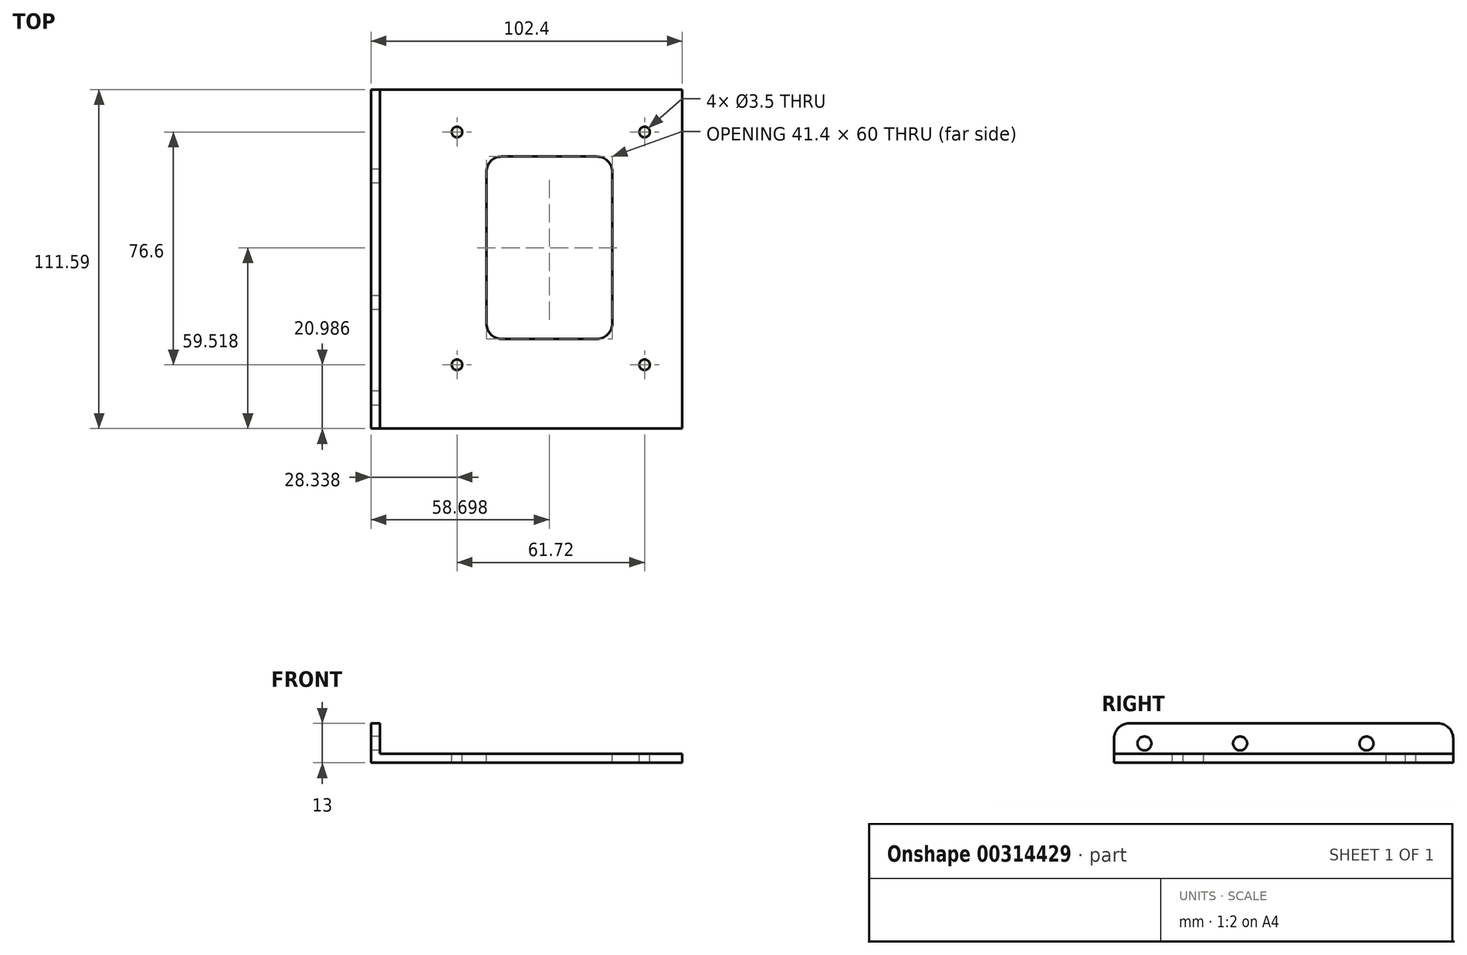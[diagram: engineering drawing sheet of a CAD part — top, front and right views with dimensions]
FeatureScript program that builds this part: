
annotation { "Feature Type Name" : "Feature", "Feature Type Description" : "" }
export const myFeature = defineFeature(function(context is Context, id is Id, definition is map)
    precondition{}
    {
        {
            var Q0;
            Q0=qCreatedBy(makeId("Top.planeOp"),FACE);
            var sketch = newSketch(context, id + "F0", { "sketchPlane" : qUnion([Q0])});
            skLineSegment(sketch, "E0.bottom", {"start": v(-63.5, 99.79) * mm, "end": v(38.9, 99.79) * mm});
            skLineSegment(sketch, "E0.top", {"start": v(-63.5, -47.21) * mm, "end": v(38.9, -47.21) * mm});
            skLineSegment(sketch, "E0.left", {"start": v(-63.5, 99.79) * mm, "end": v(-63.5, -47.21) * mm});
            skLineSegment(sketch, "E0.right", {"start": v(38.9, 99.79) * mm, "end": v(38.9, -47.21) * mm});
            skSolve(sketch);
        }
        {
            var Q0;
            Q0=qSketchRegion(id+"F0",true);
            extrude(context, id + "F1", {"entities" : qUnion([Q0]), "depth" : 3 * mm});
        }
        {
            var Q0;
            Q0=makeQuery(id+"F1.opExtrude","CAP_FACE",FACE,{"disambiguationData":[OSD([sQuery(id+"F0.wireOp",EDGE,"E0.bottom"),sQuery(id+"F0.wireOp",EDGE,"E0.top"),sQuery(id+"F0.wireOp",EDGE,"E0.left"),sQuery(id+"F0.wireOp",EDGE,"E0.right")])],"isStart":false});
            var sketch = newSketch(context, id + "F2", { "sketchPlane" : qUnion([Q0])});
            skLineSegment(sketch, "E1.bottom", {"start": v(-63.5, -47.21) * mm, "end": v(-60.5, -47.21) * mm});
            skLineSegment(sketch, "E1.top", {"start": v(-63.5, 99.79) * mm, "end": v(-60.5, 99.79) * mm});
            skLineSegment(sketch, "E1.left", {"start": v(-63.5, -47.21) * mm, "end": v(-63.5, 99.79) * mm});
            skLineSegment(sketch, "E1.right", {"start": v(-60.5, -47.21) * mm, "end": v(-60.5, 99.79) * mm});
            skSolve(sketch);
        }
        {
            var Q0;
            Q0=qSketchRegion(id+"F2",true);
            extrude(context, id + "F3", {"entities" : qUnion([Q0]), "operationType" : NewBodyOperationType.ADD, "depth" : 10 * mm});
        }
        {
            var Q0;
            Q0=makeQuery(id+"F1.opExtrude","SWEPT_FACE",FACE,{"disambiguationData":[OSD([sQuery(id+"F0.wireOp",EDGE,"E0.right")])]});
            var Q1;
            Q1=makeQuery(id+"F3.boolean.opBoolean","MERGE",FACE,{"derivedFrom":[makeQuery(id+"F1.opExtrude","SWEPT_FACE",FACE,{"disambiguationData":[OSD([sQuery(id+"F0.wireOp",EDGE,"E0.left")])]}),makeQuery(id+"F3.opExtrude","SWEPT_FACE",FACE,{"disambiguationData":[OSD([sQuery(id+"F2.wireOp",EDGE,"E1.left")])]})]});
            cPlane(context, id + "F4", {"entities" : qUnion([Q0, Q1]), "cplaneType" : CPlaneType.MID_PLANE, "offset" : 25 * mm, "width" : 150 * mm, "height" : 150 * mm});
        }
        {
            var Q0;
            Q0=makeQuery(id+"F3.boolean.opBoolean","MERGE",FACE,{"derivedFrom":[makeQuery(id+"F1.opExtrude","SWEPT_FACE",FACE,{"disambiguationData":[OSD([sQuery(id+"F0.wireOp",EDGE,"E0.left")])]}),makeQuery(id+"F3.opExtrude","SWEPT_FACE",FACE,{"disambiguationData":[OSD([sQuery(id+"F2.wireOp",EDGE,"E1.left")])]})]});
            var sketch = newSketch(context, id + "F5", { "sketchPlane" : qUnion([Q0])});
            skCircle(sketch, "E2", {"center": v(1.81, 6.35) * mm, "radius": 2.3 * mm});
            skCircle(sketch, "E3", {"center": v(-29.68, 6.35) * mm, "radius": 2.3 * mm});
            skCircle(sketch, "E4", {"center": v(-71.29, 6.35) * mm, "radius": 2.3 * mm});
            skSolve(sketch);
        }
        {
            var Q0;
            Q0=qSketchRegion(id+"F5",true);
            extrude(context, id + "F6", {"entities" : qUnion([Q0]), "operationType" : NewBodyOperationType.REMOVE, "endBound" : BoundingType.THROUGH_ALL, "oppositeDirection" : true, "depth" : 25 * mm});
        }
        {
            var Q0;
            Q0=makeQuery(id+"F1.opExtrude","CAP_FACE",FACE,{"disambiguationData":[OSD([sQuery(id+"F0.wireOp",EDGE,"E0.bottom"),sQuery(id+"F0.wireOp",EDGE,"E0.top"),sQuery(id+"F0.wireOp",EDGE,"E0.left"),sQuery(id+"F0.wireOp",EDGE,"E0.right")])],"isStart":false});
            var sketch = newSketch(context, id + "F7", { "sketchPlane" : qUnion([Q0])});
            skCircle(sketch, "E5", {"center": v(18.56, 85.79) * mm, "radius": 1.75 * mm});
            skCircle(sketch, "E6", {"center": v(-43.16, 85.79) * mm, "radius": 1.75 * mm});
            skCircle(sketch, "E7", {"center": v(18.56, 9.19) * mm, "radius": 1.75 * mm});
            skCircle(sketch, "E8", {"center": v(-43.16, 9.19) * mm, "radius": 1.75 * mm});
            skCircle(sketch, "E9.1.0.0", {"center": v(26.56, 85.79) * mm, "radius": 1.75 * mm});
            skCircle(sketch, "E9.1.0.1", {"center": v(-35.16, 85.79) * mm, "radius": 1.75 * mm});
            skCircle(sketch, "E9.1.0.2", {"center": v(-35.16, 9.19) * mm, "radius": 1.75 * mm});
            skCircle(sketch, "E9.1.0.3", {"center": v(26.56, 9.19) * mm, "radius": 1.75 * mm});
            skLineSegment(sketch, "E9.direction1", {"start": v(-43.16, 9.19) * mm, "end": v(-35.16, 9.19) * mm, "construction": true});
            skSolve(sketch);
        }
        {
            var Q0;
            Q0=makeQuery(id+"F7.imprint","IMPRINT",FACE,{"disambiguationData":[TD([[makeQuery(id+"F7.imprint","IMPRINT",EDGE,{"derivedFrom":sQuery(id+"F7.wireOp",EDGE,"E9.1.0.3")}),1.0]])]});
            var Q1;
            Q1=makeQuery(id+"F7.imprint","IMPRINT",FACE,{"disambiguationData":[TD([[makeQuery(id+"F7.imprint","IMPRINT",EDGE,{"derivedFrom":sQuery(id+"F7.wireOp",EDGE,"E9.1.0.2")}),1.0]])]});
            var Q2;
            Q2=makeQuery(id+"F7.imprint","IMPRINT",FACE,{"disambiguationData":[TD([[makeQuery(id+"F7.imprint","IMPRINT",EDGE,{"derivedFrom":sQuery(id+"F7.wireOp",EDGE,"E9.1.0.1")}),1.0]])]});
            var Q3;
            Q3=makeQuery(id+"F7.imprint","IMPRINT",FACE,{"disambiguationData":[TD([[makeQuery(id+"F7.imprint","IMPRINT",EDGE,{"derivedFrom":sQuery(id+"F7.wireOp",EDGE,"E9.1.0.0")}),1.0]])]});
            extrude(context, id + "F8", {"entities" : qUnion([Q0, Q1, Q2, Q3]), "operationType" : NewBodyOperationType.REMOVE, "endBound" : BoundingType.THROUGH_ALL, "oppositeDirection" : true, "depth" : 25 * mm});
        }
        {
            var Q0;
            Q0=makeQuery(id+"F1.opExtrude","CAP_FACE",FACE,{"disambiguationData":[OSD([sQuery(id+"F0.wireOp",EDGE,"E0.bottom"),sQuery(id+"F0.wireOp",EDGE,"E0.top"),sQuery(id+"F0.wireOp",EDGE,"E0.left"),sQuery(id+"F0.wireOp",EDGE,"E0.right")])],"isStart":false});
            var sketch = newSketch(context, id + "F9", { "sketchPlane" : qUnion([Q0])});
            skLineSegment(sketch, "E10.bottom", {"start": v(15.9, 17.72) * mm, "end": v(-25.5, 17.72) * mm});
            skLineSegment(sketch, "E10.top", {"start": v(15.9, 77.72) * mm, "end": v(-25.5, 77.72) * mm});
            skLineSegment(sketch, "E10.left", {"start": v(15.9, 17.72) * mm, "end": v(15.9, 77.72) * mm});
            skLineSegment(sketch, "E10.right", {"start": v(-25.5, 17.72) * mm, "end": v(-25.5, 77.72) * mm});
            skLineSegment(sketch, "E11.bottom", {"start": v(43.89, -51.25) * mm, "end": v(-71.44, -51.25) * mm});
            skLineSegment(sketch, "E11.top", {"start": v(43.89, -11.8) * mm, "end": v(-71.44, -11.8) * mm});
            skLineSegment(sketch, "E11.left", {"start": v(43.89, -51.25) * mm, "end": v(43.89, -11.8) * mm});
            skLineSegment(sketch, "E11.right", {"start": v(-71.44, -51.25) * mm, "end": v(-71.44, -11.8) * mm});
            skSolve(sketch);
        }
        {
            var Q0;
            Q0=makeQuery(id+"F9.imprint","IMPRINT",FACE,{"disambiguationData":[TD([[makeQuery(id+"F9.imprint","IMPRINT",EDGE,{"derivedFrom":sQuery(id+"F9.wireOp",EDGE,"E10.bottom")}),-1.0]])]});
            var Q1;
            {var subQ6=makeQuery(id+"F1.opExtrude","CAP_EDGE",EDGE,{"disambiguationData":[OSD([sQuery(id+"F0.wireOp",EDGE,"E0.top")])],"isStart":false});Q1=makeQuery(id+"F9.imprint","IMPRINT",FACE,{"disambiguationData":[TD([[makeQuery(id+"F9.imprint","IMPRINT",EDGE,{"derivedFrom":subQ6}),1.0]])]});}
            var Q2;
            Q2=makeQuery(id+"F9.imprint","IMPRINT",FACE,{"disambiguationData":[TD([[makeQuery(id+"F9.imprint","IMPRINT",EDGE,{"derivedFrom":sQuery(id+"F9.wireOp",EDGE,"E11.bottom")}),-1.0]])]});
            extrude(context, id + "F10", {"entities" : qUnion([Q0, Q1, Q2]), "operationType" : NewBodyOperationType.REMOVE, "endBound" : BoundingType.SYMMETRIC, "oppositeDirection" : true, "depth" : 25 * mm});
        }
        {
            var Q0;
            Q0=makeQuery(id+"F10.boolean.opBoolean","COPY",EDGE,{"derivedFrom":makeQuery(id+"F10.opExtrude","SWEPT_EDGE",EDGE,{"disambiguationData":[OSD([sQuery(id+"F0.wireOp",EDGE,"E0.top"),sQuery(id+"F9.wireOp",EDGE,"vKdkQJEl-uckU-Jc9d-UXZr-hBO2NRbwrfet.bottom"),sQuery(id+"F9.wireOp",EDGE,"vKdkQJEl-uckU-Jc9d-UXZr-hBO2NRbwrfet.right")])]})});
            var Q1;
            Q1=makeQuery(id+"F10.boolean.opBoolean","COPY",EDGE,{"derivedFrom":makeQuery(id+"F10.opExtrude","SWEPT_EDGE",EDGE,{"disambiguationData":[OSD([sQuery(id+"F0.wireOp",EDGE,"E0.top"),sQuery(id+"F9.wireOp",EDGE,"vKdkQJEl-uckU-Jc9d-UXZr-hBO2NRbwrfet.bottom"),sQuery(id+"F9.wireOp",EDGE,"vKdkQJEl-uckU-Jc9d-UXZr-hBO2NRbwrfet.left")])]})});
            var Q2;
            Q2=makeQuery(id+"F10.boolean.opBoolean","COPY",EDGE,{"derivedFrom":makeQuery(id+"F10.opExtrude","SWEPT_EDGE",EDGE,{"disambiguationData":[OSD([sQuery(id+"F9.wireOp",EDGE,"vKdkQJEl-uckU-Jc9d-UXZr-hBO2NRbwrfet.top"),sQuery(id+"F9.wireOp",EDGE,"vKdkQJEl-uckU-Jc9d-UXZr-hBO2NRbwrfet.left")])]})});
            var Q3;
            Q3=makeQuery(id+"FGaxl9y5x9EvqOz_1.1.F3.opExtrude","CAP_EDGE",EDGE,{"disambiguationData":[OSD([sQuery(id+"F2.wireOp",EDGE,"E1.bottom")])],"isStart":false});
            var Q4;
            Q4=makeQuery(id+"F10.boolean.opBoolean","COPY",EDGE,{"derivedFrom":makeQuery(id+"F10.opExtrude","SWEPT_EDGE",EDGE,{"disambiguationData":[OSD([sQuery(id+"F9.wireOp",EDGE,"vKdkQJEl-uckU-Jc9d-UXZr-hBO2NRbwrfet.top"),sQuery(id+"F9.wireOp",EDGE,"vKdkQJEl-uckU-Jc9d-UXZr-hBO2NRbwrfet.right")])]})});
            var Q5;
            Q5=makeQuery(id+"F3.opExtrude","CAP_EDGE",EDGE,{"disambiguationData":[OSD([sQuery(id+"F2.wireOp",EDGE,"E1.bottom")])],"isStart":false});
            var Q6;
            Q6=makeQuery(id+"F3.opExtrude","CAP_EDGE",EDGE,{"disambiguationData":[OSD([sQuery(id+"F2.wireOp",EDGE,"E1.top")])],"isStart":false});
            var Q7;
            Q7=makeQuery(id+"FGaxl9y5x9EvqOz_1.1.F3.opExtrude","CAP_EDGE",EDGE,{"disambiguationData":[OSD([sQuery(id+"F2.wireOp",EDGE,"E1.top")])],"isStart":false});
            var Q8;
            Q8=makeQuery(id+"F10.boolean.opBoolean","INTERSECT",EDGE,{"derivedFrom":[makeQuery(id+"FGaxl9y5x9EvqOz_1.1.F3.opExtrude","CAP_FACE",FACE,{"disambiguationData":[OSD([sQuery(id+"F2.wireOp",EDGE,"E1.bottom"),sQuery(id+"F2.wireOp",EDGE,"E1.top"),sQuery(id+"F2.wireOp",EDGE,"E1.left"),sQuery(id+"F2.wireOp",EDGE,"E1.right")])],"isStart":false}),makeQuery(id+"F10.opExtrude","SWEPT_FACE",FACE,{"disambiguationData":[OSD([sQuery(id+"F9.wireOp",EDGE,"E11.top")])]})]});
            var Q9;
            Q9=makeQuery(id+"F10.boolean.opBoolean","INTERSECT",EDGE,{"derivedFrom":[makeQuery(id+"F3.opExtrude","CAP_FACE",FACE,{"disambiguationData":[OSD([sQuery(id+"F2.wireOp",EDGE,"E1.bottom"),sQuery(id+"F2.wireOp",EDGE,"E1.top"),sQuery(id+"F2.wireOp",EDGE,"E1.left"),sQuery(id+"F2.wireOp",EDGE,"E1.right")])],"isStart":false}),makeQuery(id+"F10.opExtrude","SWEPT_FACE",FACE,{"disambiguationData":[OSD([sQuery(id+"F9.wireOp",EDGE,"E11.top")])]})]});
            var Q10;
            Q10=makeQuery(id+"F10.boolean.opBoolean","COPY",EDGE,{"derivedFrom":makeQuery(id+"F10.opExtrude","SWEPT_EDGE",EDGE,{"disambiguationData":[OSD([sQuery(id+"F9.wireOp",EDGE,"E10.bottom"),sQuery(id+"F9.wireOp",EDGE,"E10.left")])]})});
            var Q11;
            Q11=makeQuery(id+"F10.boolean.opBoolean","COPY",EDGE,{"derivedFrom":makeQuery(id+"F10.opExtrude","SWEPT_EDGE",EDGE,{"disambiguationData":[OSD([sQuery(id+"F9.wireOp",EDGE,"E10.bottom"),sQuery(id+"F9.wireOp",EDGE,"E10.right")])]})});
            var Q12;
            Q12=makeQuery(id+"F10.boolean.opBoolean","COPY",EDGE,{"derivedFrom":makeQuery(id+"F10.opExtrude","SWEPT_EDGE",EDGE,{"disambiguationData":[OSD([sQuery(id+"F9.wireOp",EDGE,"E10.top"),sQuery(id+"F9.wireOp",EDGE,"E10.right")])]})});
            var Q13;
            Q13=makeQuery(id+"F10.boolean.opBoolean","COPY",EDGE,{"derivedFrom":makeQuery(id+"F10.opExtrude","SWEPT_EDGE",EDGE,{"disambiguationData":[OSD([sQuery(id+"F9.wireOp",EDGE,"E10.top"),sQuery(id+"F9.wireOp",EDGE,"E10.left")])]})});
            fillet(context, id + "F11", {"entities" : qUnion([Q0, Q1, Q2, Q3, Q4, Q5, Q6, Q7, Q8, Q9, Q10, Q11, Q12, Q13]), "radius" : 5 * mm, "tangentPropagation" : true, "allowEdgeOverflow" : false});
        }
    });
